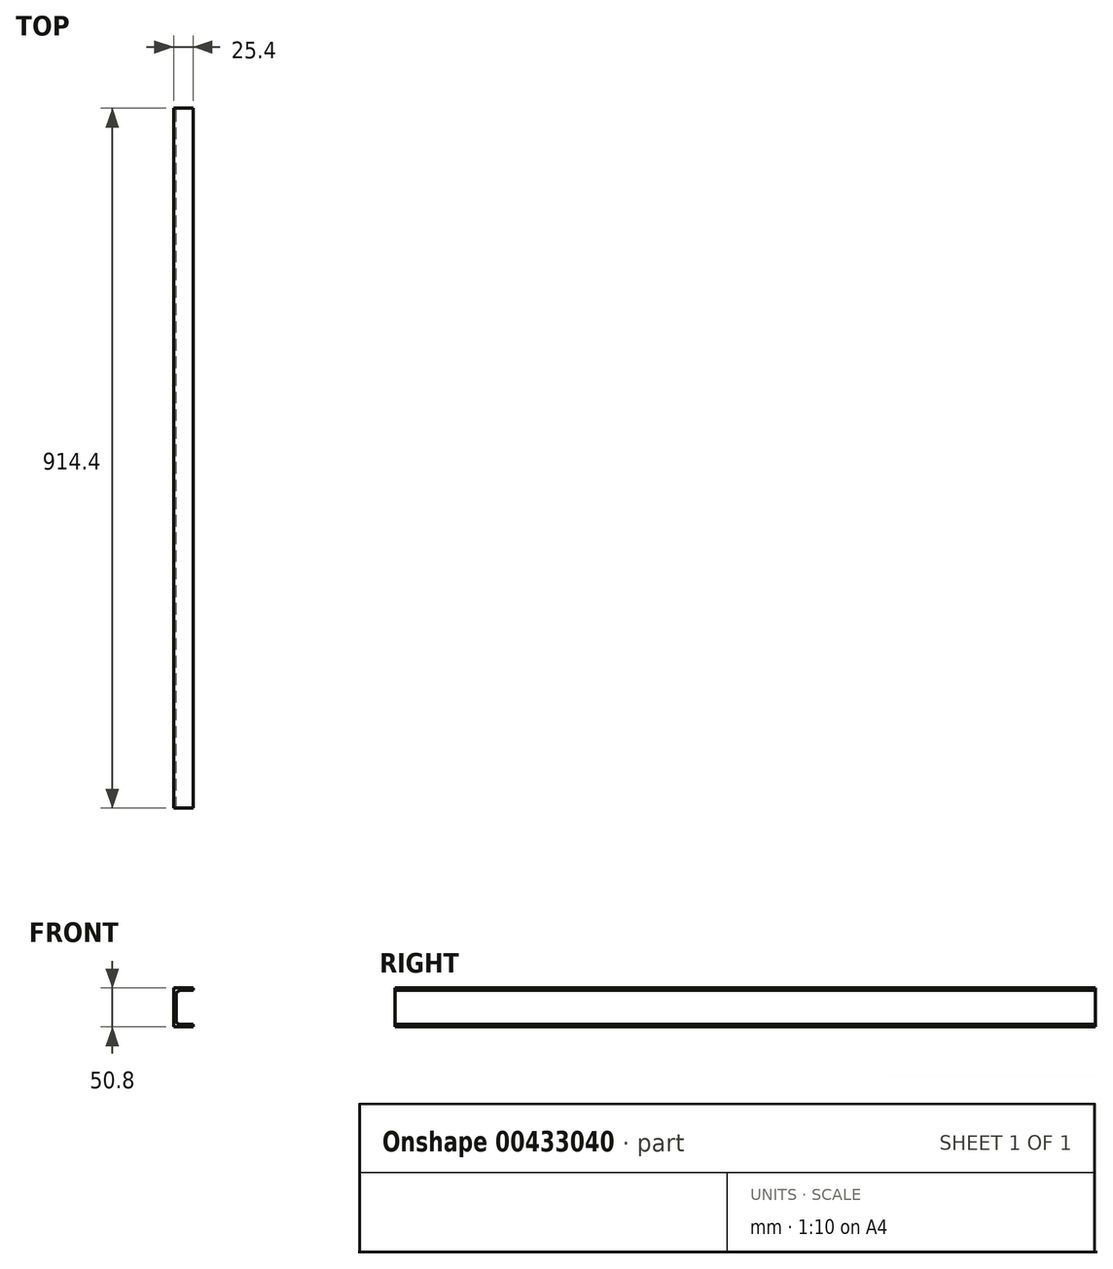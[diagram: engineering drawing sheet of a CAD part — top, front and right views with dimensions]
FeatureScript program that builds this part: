
annotation { "Feature Type Name" : "Feature", "Feature Type Description" : "" }
export const myFeature = defineFeature(function(context is Context, id is Id, definition is map)
    precondition{}
    {
        {
            var Q0;
            Q0=qCreatedBy(makeId("Front.planeOp"),FACE);
            var sketch = newSketch(context, id + "F0", { "sketchPlane" : qUnion([Q0])});
            skLineSegment(sketch, "E0", {"start": v(0, 0) * mm, "end": v(0, 50.8) * mm});
            skLineSegment(sketch, "E1", {"start": v(0, 50.8) * mm, "end": v(25.4, 50.8) * mm});
            skLineSegment(sketch, "E2", {"start": v(25.4, 50.8) * mm, "end": v(25.4, 47.63) * mm});
            skLineSegment(sketch, "E3", {"start": v(25.4, 47.63) * mm, "end": v(9.52, 47.63) * mm});
            skLineSegment(sketch, "E4", {"start": v(3.17, 41.28) * mm, "end": v(3.18, 9.52) * mm});
            skLineSegment(sketch, "E5", {"start": v(9.53, 3.17) * mm, "end": v(25.4, 3.18) * mm});
            skLineSegment(sketch, "E6", {"start": v(25.4, 3.18) * mm, "end": v(25.4, 0) * mm});
            skLineSegment(sketch, "E7", {"start": v(25.4, 0) * mm, "end": v(0, 0) * mm});
            skPoint(sketch, "E8.visualSharp", {"position": v(3.17, 47.63) * mm});
            skArc(sketch, "E8.filletArc", {"start": v(9.52, 47.63) * mm, "mid": v(5.03, 45.77) * mm, "end": v(3.17, 41.28) * mm});
            skPoint(sketch, "E9.visualSharp", {"position": v(3.18, 3.17) * mm});
            skArc(sketch, "E9.filletArc", {"start": v(3.18, 9.53) * mm, "mid": v(5.03, 5.03) * mm, "end": v(9.53, 3.17) * mm});
            skSolve(sketch);
        }
        {
            var Q0;
            Q0=makeQuery(id+"F0.imprint","IMPRINT",FACE,{"disambiguationData":[TD([[makeQuery(id+"F0.imprint","IMPRINT",EDGE,{"derivedFrom":sQuery(id+"F0.wireOp",EDGE,"E0")}),-1.0]])]});
            extrude(context, id + "F1", {"entities" : qUnion([Q0]), "depth" : 914.4 * mm, "offsetDistance" : 25.4 * mm});
        }
    });
